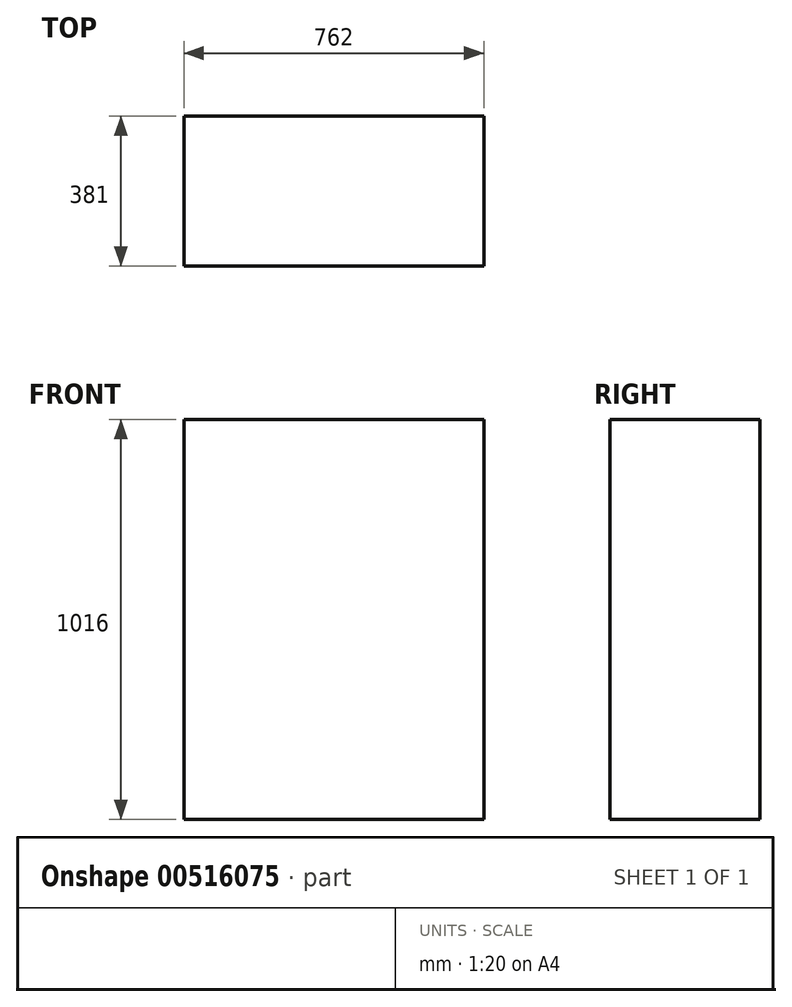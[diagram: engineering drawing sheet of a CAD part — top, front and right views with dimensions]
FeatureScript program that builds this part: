
annotation { "Feature Type Name" : "Feature", "Feature Type Description" : "" }
export const myFeature = defineFeature(function(context is Context, id is Id, definition is map)
    precondition{}
    {
        {
            var Q0;
            Q0=qCreatedBy(makeId("Top.planeOp"),FACE);
            var sketch = newSketch(context, id + "F0", { "sketchPlane" : qUnion([Q0])});
            skLineSegment(sketch, "E0.bottom", {"start": v(381, -190.5) * mm, "end": v(-381, -190.5) * mm});
            skLineSegment(sketch, "E0.top", {"start": v(381, 190.5) * mm, "end": v(-381, 190.5) * mm});
            skLineSegment(sketch, "E0.left", {"start": v(381, -190.5) * mm, "end": v(381, 190.5) * mm});
            skLineSegment(sketch, "E0.right", {"start": v(-381, -190.5) * mm, "end": v(-381, 190.5) * mm});
            skPoint(sketch, "E0.middle", {"position": v(0, 0) * mm});
            skSolve(sketch);
        }
        {
            var Q0;
            Q0=makeQuery(id+"F0.imprint","IMPRINT",FACE,{"disambiguationData":[TD([[makeQuery(id+"F0.imprint","IMPRINT",EDGE,{"derivedFrom":sQuery(id+"F0.wireOp",EDGE,"E0.bottom")}),-1.0]])]});
            extrude(context, id + "F1", {"entities" : qUnion([Q0]), "depth" : 1016 * mm, "offsetDistance" : 25.4 * mm});
        }
    });
